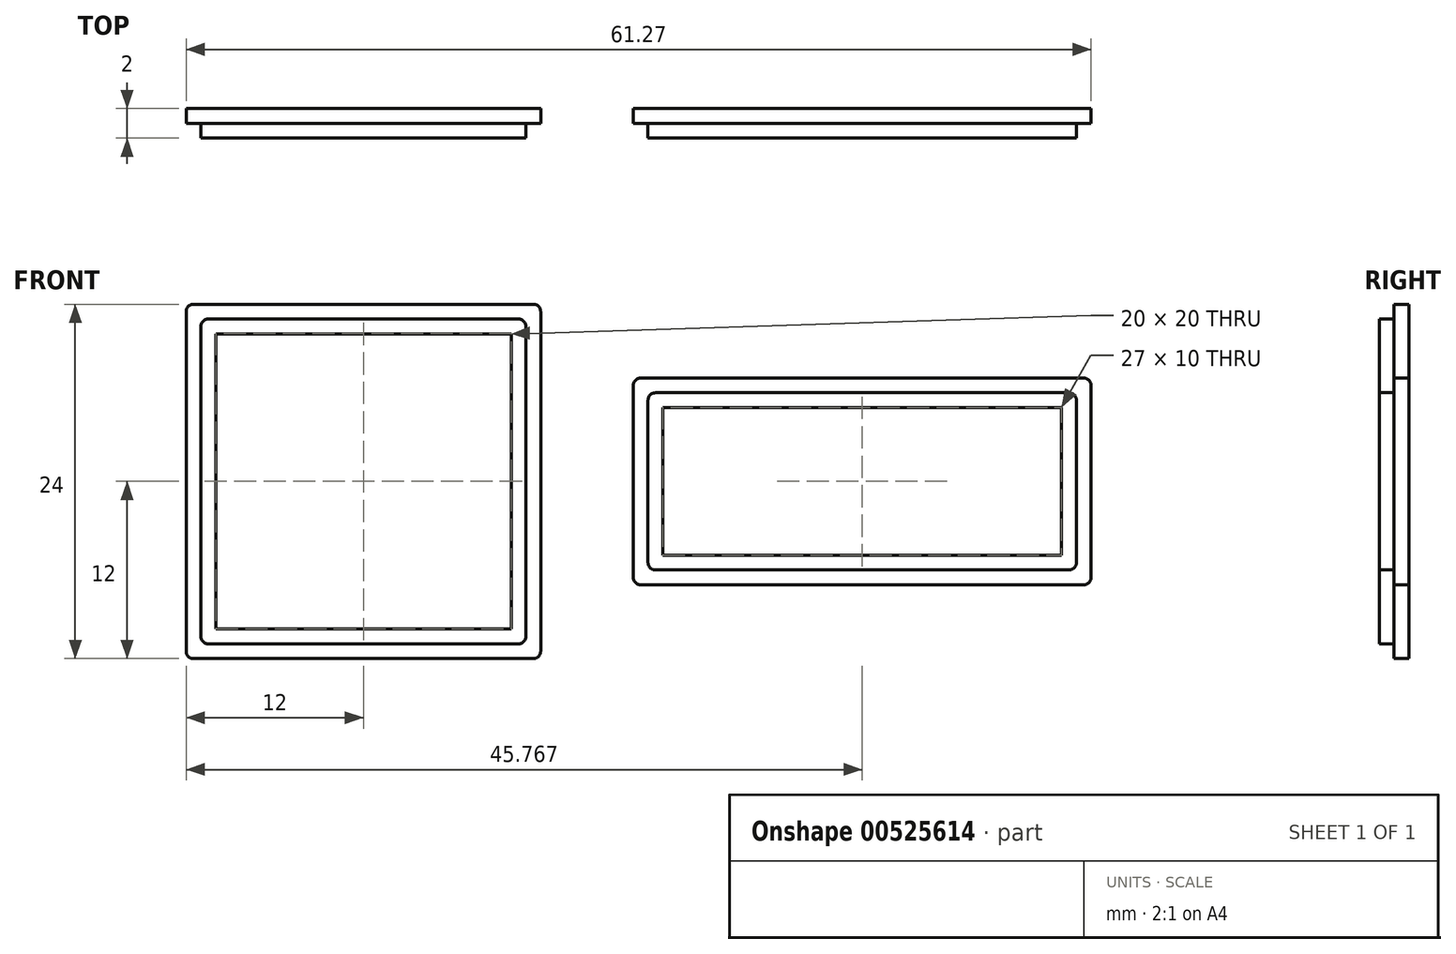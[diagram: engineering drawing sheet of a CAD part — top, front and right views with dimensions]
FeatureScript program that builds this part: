
annotation { "Feature Type Name" : "Feature", "Feature Type Description" : "" }
export const myFeature = defineFeature(function(context is Context, id is Id, definition is map)
    precondition{}
    {
        {
            var Q0;
            Q0=qCreatedBy(makeId("Front.planeOp"),FACE);
            cPlane(context, id + "F0", {"entities" : qUnion([Q0]), "cplaneType" : CPlaneType.OFFSET, "offset" : 1 * mm, "width" : 150 * mm, "height" : 150 * mm});
        }
        {
            var Q0;
            Q0=qCreatedBy(id+"F0.planeOp",FACE);
            var sketch = newSketch(context, id + "F1", { "sketchPlane" : qUnion([Q0])});
            skLineSegment(sketch, "E0.bottom", {"start": v(12, -12) * mm, "end": v(-12, -12) * mm});
            skLineSegment(sketch, "E0.top", {"start": v(12, 12) * mm, "end": v(-12, 12) * mm});
            skLineSegment(sketch, "E0.left", {"start": v(12, -12) * mm, "end": v(12, 12) * mm});
            skLineSegment(sketch, "E0.right", {"start": v(-12, -12) * mm, "end": v(-12, 12) * mm});
            skPoint(sketch, "E0.middle", {"position": v(0, 0) * mm});
            skLineSegment(sketch, "E1.bottom", {"start": v(10, -10) * mm, "end": v(-10, -10) * mm});
            skLineSegment(sketch, "E1.top", {"start": v(10, 10) * mm, "end": v(-10, 10) * mm});
            skLineSegment(sketch, "E1.left", {"start": v(10, -10) * mm, "end": v(10, 10) * mm});
            skLineSegment(sketch, "E1.right", {"start": v(-10, -10) * mm, "end": v(-10, 10) * mm});
            skLineSegment(sketch, "E2.bottom", {"start": v(47.27, -5) * mm, "end": v(20.27, -5) * mm});
            skLineSegment(sketch, "E2.top", {"start": v(47.27, 5) * mm, "end": v(20.27, 5) * mm});
            skLineSegment(sketch, "E2.left", {"start": v(47.27, -5) * mm, "end": v(47.27, 5) * mm});
            skLineSegment(sketch, "E2.right", {"start": v(20.27, -5) * mm, "end": v(20.27, 5) * mm});
            skPoint(sketch, "E2.middle", {"position": v(33.77, 0) * mm});
            skLineSegment(sketch, "E3.bottom", {"start": v(49.27, -7) * mm, "end": v(18.27, -7) * mm});
            skLineSegment(sketch, "E3.top", {"start": v(49.27, 7) * mm, "end": v(18.27, 7) * mm});
            skLineSegment(sketch, "E3.left", {"start": v(49.27, -7) * mm, "end": v(49.27, 7) * mm});
            skLineSegment(sketch, "E3.right", {"start": v(18.27, -7) * mm, "end": v(18.27, 7) * mm});
            skSolve(sketch);
        }
        {
            var Q0;
            Q0=qSketchRegion(id+"F1",true);
            extrude(context, id + "F2", {"entities" : qUnion([Q0]), "depth" : 2 * mm, "offsetDistance" : 25 * mm});
        }
        {
            var Q0;
            Q0=makeQuery(id+"F2.opExtrude","CAP_FACE",FACE,{"disambiguationData":[OSD([sQuery(id+"F1.wireOp",EDGE,"E0.bottom"),sQuery(id+"F1.wireOp",EDGE,"E0.top"),sQuery(id+"F1.wireOp",EDGE,"E0.left"),sQuery(id+"F1.wireOp",EDGE,"E0.right"),sQuery(id+"F1.wireOp",EDGE,"E1.bottom"),sQuery(id+"F1.wireOp",EDGE,"E1.top"),sQuery(id+"F1.wireOp",EDGE,"E1.left"),sQuery(id+"F1.wireOp",EDGE,"E1.right")])],"isStart":false});
            var sketch = newSketch(context, id + "F3", { "sketchPlane" : qUnion([Q0])});
            skLineSegment(sketch, "E4.bottom", {"start": v(12, -12) * mm, "end": v(-12, -12) * mm});
            skLineSegment(sketch, "E4.top", {"start": v(12, 12) * mm, "end": v(-12, 12) * mm});
            skLineSegment(sketch, "E4.left", {"start": v(12, -12) * mm, "end": v(12, 12) * mm});
            skLineSegment(sketch, "E4.right", {"start": v(-12, -12) * mm, "end": v(-12, 12) * mm});
            skPoint(sketch, "E4.middle", {"position": v(0, 0) * mm});
            skLineSegment(sketch, "E5.bottom", {"start": v(11, -11) * mm, "end": v(-11, -11) * mm});
            skLineSegment(sketch, "E5.top", {"start": v(11, 11) * mm, "end": v(-11, 11) * mm});
            skLineSegment(sketch, "E5.left", {"start": v(11, -11) * mm, "end": v(11, 11) * mm});
            skLineSegment(sketch, "E5.right", {"start": v(-11, -11) * mm, "end": v(-11, 11) * mm});
            skLineSegment(sketch, "E6.bottom", {"start": v(49.27, -7) * mm, "end": v(18.27, -7) * mm});
            skLineSegment(sketch, "E6.top", {"start": v(49.27, 7) * mm, "end": v(18.27, 7) * mm});
            skLineSegment(sketch, "E6.left", {"start": v(49.27, -7) * mm, "end": v(49.27, 7) * mm});
            skLineSegment(sketch, "E6.right", {"start": v(18.27, -7) * mm, "end": v(18.27, 7) * mm});
            skPoint(sketch, "E6.middle", {"position": v(33.77, 0) * mm});
            skLineSegment(sketch, "E7.bottom", {"start": v(48.27, -6) * mm, "end": v(19.27, -6) * mm});
            skLineSegment(sketch, "E7.top", {"start": v(48.27, 6) * mm, "end": v(19.27, 6) * mm});
            skLineSegment(sketch, "E7.left", {"start": v(48.27, -6) * mm, "end": v(48.27, 6) * mm});
            skLineSegment(sketch, "E7.right", {"start": v(19.27, -6) * mm, "end": v(19.27, 6) * mm});
            skSolve(sketch);
        }
        {
            var Q0;
            Q0=qSketchRegion(id+"F3",true);
            extrude(context, id + "F4", {"entities" : qUnion([Q0]), "operationType" : NewBodyOperationType.REMOVE, "oppositeDirection" : true, "depth" : 1 * mm, "offsetDistance" : 25 * mm});
        }
        {
            var Q0;
            Q0=makeQuery(id+"F2.opExtrude","SWEPT_EDGE",EDGE,{"disambiguationData":[OSD([sQuery(id+"F1.wireOp",EDGE,"E0.top"),sQuery(id+"F1.wireOp",EDGE,"E0.right")])]});
            var Q1;
            Q1=makeQuery(id+"F4.boolean.opBoolean","COPY",EDGE,{"derivedFrom":makeQuery(id+"F4.opExtrude","SWEPT_EDGE",EDGE,{"disambiguationData":[OSD([sQuery(id+"F3.wireOp",EDGE,"E5.top"),sQuery(id+"F3.wireOp",EDGE,"E5.right")])]})});
            var Q2;
            Q2=makeQuery(id+"F4.boolean.opBoolean","COPY",EDGE,{"derivedFrom":makeQuery(id+"F4.opExtrude","SWEPT_EDGE",EDGE,{"disambiguationData":[OSD([sQuery(id+"F3.wireOp",EDGE,"E5.bottom"),sQuery(id+"F3.wireOp",EDGE,"E5.right")])]})});
            var Q3;
            Q3=makeQuery(id+"F2.opExtrude","SWEPT_EDGE",EDGE,{"disambiguationData":[OSD([sQuery(id+"F1.wireOp",EDGE,"E0.bottom"),sQuery(id+"F1.wireOp",EDGE,"E0.right")])]});
            var Q4;
            Q4=makeQuery(id+"F4.boolean.opBoolean","COPY",EDGE,{"derivedFrom":makeQuery(id+"F4.opExtrude","SWEPT_EDGE",EDGE,{"disambiguationData":[OSD([sQuery(id+"F3.wireOp",EDGE,"E5.bottom"),sQuery(id+"F3.wireOp",EDGE,"E5.left")])]})});
            var Q5;
            Q5=makeQuery(id+"F2.opExtrude","SWEPT_EDGE",EDGE,{"disambiguationData":[OSD([sQuery(id+"F1.wireOp",EDGE,"E0.bottom"),sQuery(id+"F1.wireOp",EDGE,"E0.left")])]});
            var Q6;
            Q6=makeQuery(id+"F2.opExtrude","SWEPT_EDGE",EDGE,{"disambiguationData":[OSD([sQuery(id+"F1.wireOp",EDGE,"E0.top"),sQuery(id+"F1.wireOp",EDGE,"E0.left")])]});
            var Q7;
            Q7=makeQuery(id+"F4.boolean.opBoolean","COPY",EDGE,{"derivedFrom":makeQuery(id+"F4.opExtrude","SWEPT_EDGE",EDGE,{"disambiguationData":[OSD([sQuery(id+"F3.wireOp",EDGE,"E5.top"),sQuery(id+"F3.wireOp",EDGE,"E5.left")])]})});
            var Q8;
            Q8=makeQuery(id+"F2.opExtrude","SWEPT_EDGE",EDGE,{"disambiguationData":[OSD([sQuery(id+"F1.wireOp",EDGE,"E3.bottom"),sQuery(id+"F1.wireOp",EDGE,"E3.right")])]});
            var Q9;
            Q9=makeQuery(id+"F4.boolean.opBoolean","COPY",EDGE,{"derivedFrom":makeQuery(id+"F4.opExtrude","SWEPT_EDGE",EDGE,{"disambiguationData":[OSD([sQuery(id+"F3.wireOp",EDGE,"E7.bottom"),sQuery(id+"F3.wireOp",EDGE,"E7.right")])]})});
            var Q10;
            Q10=makeQuery(id+"F2.opExtrude","SWEPT_EDGE",EDGE,{"disambiguationData":[OSD([sQuery(id+"F1.wireOp",EDGE,"E3.top"),sQuery(id+"F1.wireOp",EDGE,"E3.right")])]});
            var Q11;
            Q11=makeQuery(id+"F4.boolean.opBoolean","COPY",EDGE,{"derivedFrom":makeQuery(id+"F4.opExtrude","SWEPT_EDGE",EDGE,{"disambiguationData":[OSD([sQuery(id+"F3.wireOp",EDGE,"E7.top"),sQuery(id+"F3.wireOp",EDGE,"E7.right")])]})});
            var Q12;
            Q12=makeQuery(id+"F4.boolean.opBoolean","COPY",EDGE,{"derivedFrom":makeQuery(id+"F4.opExtrude","SWEPT_EDGE",EDGE,{"disambiguationData":[OSD([sQuery(id+"F3.wireOp",EDGE,"E7.bottom"),sQuery(id+"F3.wireOp",EDGE,"E7.left")])]})});
            var Q13;
            Q13=makeQuery(id+"F2.opExtrude","SWEPT_EDGE",EDGE,{"disambiguationData":[OSD([sQuery(id+"F1.wireOp",EDGE,"E3.bottom"),sQuery(id+"F1.wireOp",EDGE,"E3.left")])]});
            var Q14;
            Q14=makeQuery(id+"F2.opExtrude","SWEPT_EDGE",EDGE,{"disambiguationData":[OSD([sQuery(id+"F1.wireOp",EDGE,"E3.top"),sQuery(id+"F1.wireOp",EDGE,"E3.left")])]});
            var Q15;
            Q15=makeQuery(id+"F4.boolean.opBoolean","COPY",EDGE,{"derivedFrom":makeQuery(id+"F4.opExtrude","SWEPT_EDGE",EDGE,{"disambiguationData":[OSD([sQuery(id+"F3.wireOp",EDGE,"E7.top"),sQuery(id+"F3.wireOp",EDGE,"E7.left")])]})});
            fillet(context, id + "F5", {"entities" : qUnion([Q0, Q1, Q2, Q3, Q4, Q5, Q6, Q7, Q8, Q9, Q10, Q11, Q12, Q13, Q14, Q15]), "radius" : 0.5 * mm, "tangentPropagation" : true, "allowEdgeOverflow" : false});
        }
    });
